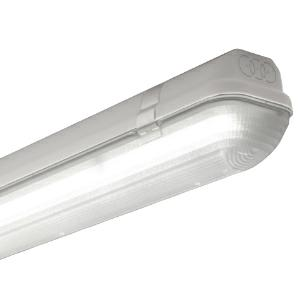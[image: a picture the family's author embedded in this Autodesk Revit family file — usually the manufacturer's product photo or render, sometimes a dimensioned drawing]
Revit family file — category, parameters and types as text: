
# Revit family: 3f_filippi_-_3f_linda_3f_filippi_-_58612_-_3f_linda_led_1x30w-865_ep_l1570
name_source: partatom
category: Lighting Fixtures
units: mm (PartAtom-declared; Revit-internal decimal feet)

## family parameters
Cut with Voids When Loaded = No
Host = Face
Light Source = No
Part Type = Normal
Room Calculation Point = No
Round Connector Dimension = Use Diameter
Shared = No

## types (1)
- 3F Filippi - 3F Linda (1 x LED, 5180 lm, 34.5 W, 6500 K)
    Apparent Load = 35 VA
    Approval mark = ENEC
    CIE Flux Codes = 44 77 94 97 100
    Color Rendering = 80
    Color Temperature = 6500 K
    Control Gear = Electronic ballast
    Default Elevation = 1800 mm
    Description = ILLUMINOTECHNICAL
Luminous efficiency 100% (DLOR 97%, ULOR 3%).
Initial luminous flux of the luminaire 5180 lm.
Emergency luminaire luminous flux BLF 11.4%.
Controlled symmetric distribution.
Installation Interdistance Transv.D = 1.77 x hu - Long.D = 1.17 x hu.
Tabular UGR (CIE 117 - 4H-8H; S=0.25H; 70/50/20): RUG 22.1 - 23.1.
Beam angle: 109° - 64°.
Luminous efficacy 150 lm/W.
Lifetime (L93/B10): 30000 h. (tq+25°C)
Lifetime (L90/B10): 50000 h. (tq+25°C)
Lifetime (L85/B10): 80000 h. (tq+25°C)
Lifetime (L80/B10): 100000 h. (tq+25°C)
Sudden decreased luminous flux after 50000 hours: 0% (C0).
Photobiological safety in compliance with IEC/TR 62778: RG0 risk exempt, (IEC 62471).
In compliance with IEC/EN 62722-2-1 - IEC/EN 62717 standards.

SOURCE
Linear LED module 30W/865.
Energy efficiency class (UE 2019/2020 - UE 2019/2015): D.
CIE 13.3 Colour rendering index: CRI >80 (R9 <50%).
IES TM-30 Fidelity Index: Rf = 84 Rg = 95.
CCT nominal colour temperature 6500 K.
Colour initial tolerance (MacAdam): SDCM 3.

MECHANICAL
Self-extinguishing V2 polycarbonate housing, injection moulded, RAL 7035 grey.
Ecologic anti-aging injected sealing gasket.
Diffuser in self-extinguishing V2 polycarbonate, photo-engraved interior, UV stabilised, injection moulded with smooth outer surface, tamper-proof opening.
Gear-holder reflector in hot-dip galvanised steel, painted with white polyester base.
Snug fit safety snap-lock clips for diffuser mounting in stainless steel, screwdriver opening.
Fixing brackets in stainless steel.
Possibility for technicians to access the interior of the luminaire.
Luminaire with limited surface temperature. - D - (EN 60598-2-24)
Dimensions: 1570x100 mm, height 100 mm. Weight 2.97 kg.
IP66 protection degree.
Mechanical strength to impacts IK10 (20 joule).
Glow-wire test resistance 850°C.

ELECTRICAL
Halogen Free electronic wiring 230V-50/60Hz, power factor 0.90, THD <25%, constant output current, SELV, class I, 1 driver.
Power of the luminaire 34.5 W.
CE - IEC 60598-1 - EN 60598-1.
EP maintained emergency wiring on board, 1h duration, 24h recharge; compliant with EN 60598-2-22, excluding high risk areas.
SAFE FLICKER: PstLM=<1 and SVM=<0.4 (IEC TR 61547-1 and IEC TR 63158), to ensure a more comfortable and safe light.
Ambient temperature from +5°C to +25°C.
Temperature class T6 max 85°C.
Relative humidity UR: <85%.

INSTALLATION
Ceiling / Suspended / Wall.
All accessories dedicated to this product are available on the Catalog and on our website www.3F-Filippi.com.

APPLICATIONS
Suitable product for food production plants (HACCP), IFS (Food Version 6), BRC (GSFS Food Version 7).
Dry, dusty indoor environments, subject to occasional water splashes.
Virtually shatterproof polycarbonate compatibly with the fumes / atmospheres that compromise the elasticity of plastic materials.
Not suitable for installation on surfaces subject to important vibrations, exposed to weather conditions, on ropes or poles.
Suitable for illumination of public car parks and parking grounds referred to DIN 67528:2018-04.

WARNING
Fixture not suitable for cold stores with an ambient temperature <5°C and/or relative humidity >85%.
Luminaire designed for disposal/recycling at end-of-life.
Replaceable (LED only) light source by a professional. Replaceable control gear by a professional.
    Height = 100 mm  [stored 0.328084 ft]
    Lamp = 1 x LED
    Lamp Light Flux = 5180 lm
    Lamp Power = 34.5 W
    Lamp count = 1
    Length = 1570 mm
    Lifetime = 50000 h
    Luminous efficacy = 150 lm/W
    Manufacturer = 3F Filippi
    ModVariant = No
    Model = 3F Filippi - 58612 - 3F Linda LED 1x30W-865 EP L1570
    Mounting Place = Ceiling
    Mounting Type = Pendant
    Number of Poles = 1
    OnlyDefault = Yes
    Power Factor = 1
    Product Name = 3F Filippi - 3F Linda
    Product group = pendant luminaire
    ProductGroupID = 9
    Protection Class = Protection class I
    Protection Degree = IP 66
    RLX_Detail_Level = 1
    RLX_Emergency_Light_Flux = 0 lm
    RLX_Emergency_Type = 0
    RLX_Emergency_Type_DB = No
    RlxData = <blob elided: 71201 chars, md5=dead5dd8>
    Socket = socket
    Standby Power = 0 W
    System Light Flux = 5180 lm
    System Power = 35 W
    Type Comments = Product without accessories
    Type Image = 3ffilippi_3f_linda_led.jpg
    URL = http://relux.com
    VarID = ---
    Voltage = 0 V
    Weight = 0.00 kg
    Width = 100 mm  [stored 0.328084 ft]

note: [stored X ft] marks values corroborated as IEEE doubles in the binary element streams (Revit-internal decimal feet)

## geometry (parser evidence)
native form markers: Blend x4, Sweep x8
no freeform markers — native parametric forms only
